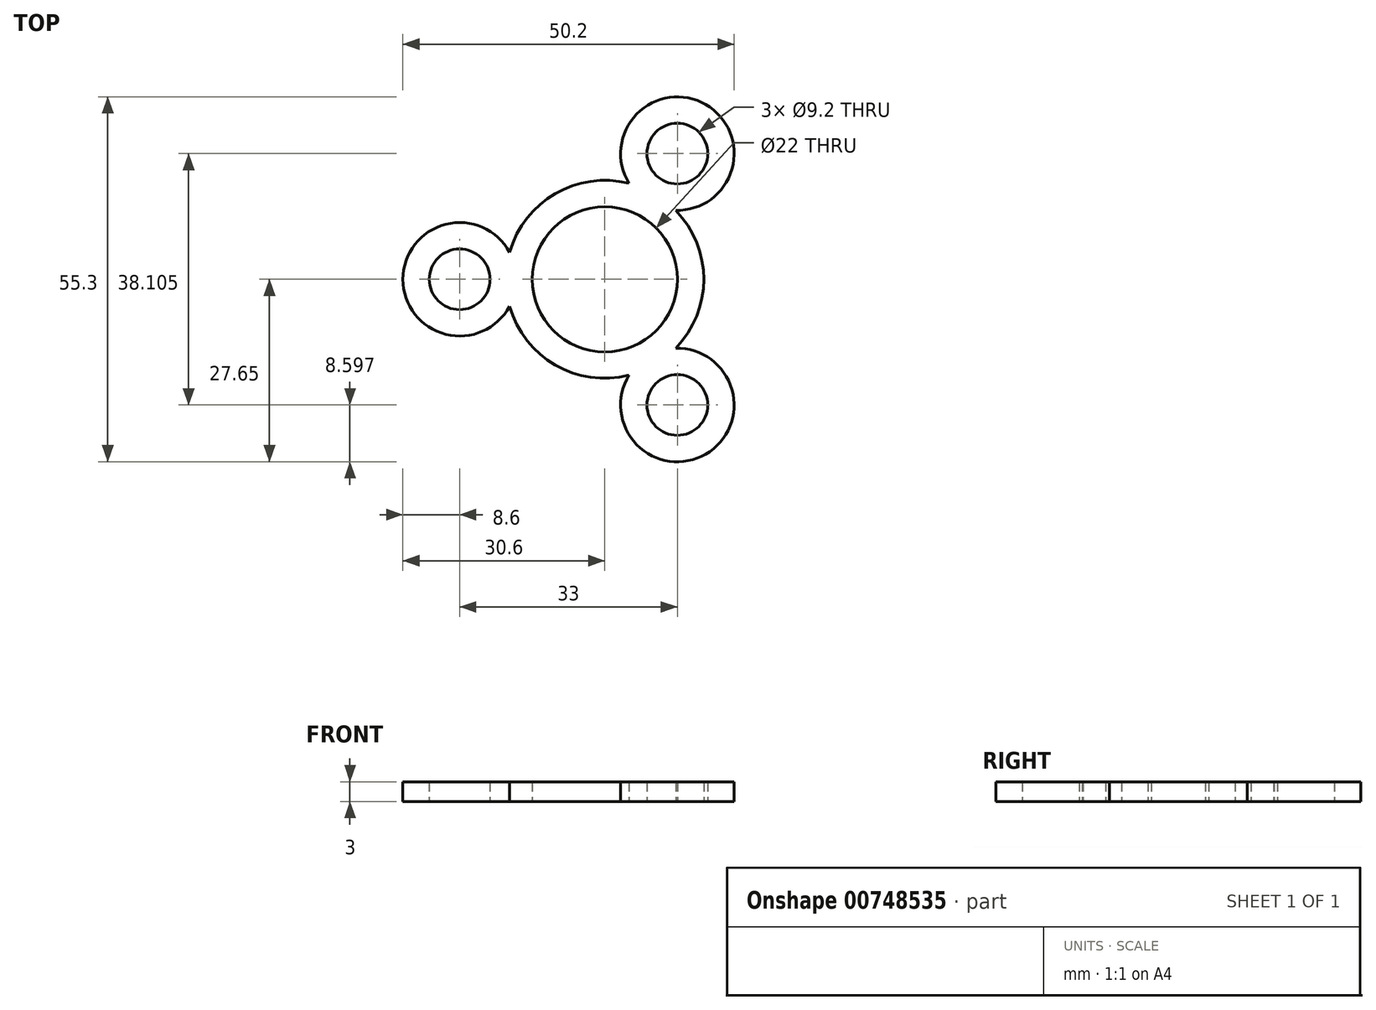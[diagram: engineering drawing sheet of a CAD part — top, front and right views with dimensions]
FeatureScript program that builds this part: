
annotation { "Feature Type Name" : "Feature", "Feature Type Description" : "" }
export const myFeature = defineFeature(function(context is Context, id is Id, definition is map)
    precondition{}
    {
        {
            var Q0;
            Q0=qCreatedBy(makeId("Top.planeOp"),FACE);
            var sketch = newSketch(context, id + "F0", { "sketchPlane" : qUnion([Q0])});
            skCircle(sketch, "E0", {"center": v(0, 0) * mm, "radius": 11 * mm});
            skArc(sketch, "E1", {"start": v(-14.43, -4.09) * mm, "mid": v(-7.5, -13) * mm, "end": v(3.68, -14.54) * mm});
            skLineSegment(sketch, "E2", {"start": v(0, 0) * mm, "end": v(-22, 0) * mm});
            skCircle(sketch, "E3", {"center": v(-22, 0) * mm, "radius": 4.6 * mm});
            skArc(sketch, "E4", {"start": v(-14.43, 4.09) * mm, "mid": v(-30.6, 0) * mm, "end": v(-14.43, -4.09) * mm});
            skArc(sketch, "E5.1.1", {"start": v(3.68, -14.54) * mm, "mid": v(15.3, -26.5) * mm, "end": v(10.76, -10.46) * mm});
            skCircle(sketch, "E5.1.2", {"center": v(11, -19.05) * mm, "radius": 4.6 * mm});
            skArc(sketch, "E5.2.1", {"start": v(10.76, 10.46) * mm, "mid": v(15.3, 26.5) * mm, "end": v(3.68, 14.54) * mm});
            skCircle(sketch, "E5.2.2", {"center": v(11, 19.05) * mm, "radius": 4.6 * mm});
            skArc(sketch, "E6.trimOffspring", {"start": v(3.68, 14.54) * mm, "mid": v(-7.5, 13) * mm, "end": v(-14.43, 4.09) * mm});
            skArc(sketch, "E7.trimOffspring", {"start": v(10.76, -10.46) * mm, "mid": v(15, 0) * mm, "end": v(10.76, 10.46) * mm});
            skSolve(sketch);
        }
        {
            var Q0;
            Q0 = qSketchRegion(id + "F0", true);
            extrude(context, id + "F1", {"entities" : qUnion([Q0]), "depth" : 3 * mm, "offsetDistance" : 25 * mm});
        }
    });
